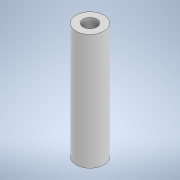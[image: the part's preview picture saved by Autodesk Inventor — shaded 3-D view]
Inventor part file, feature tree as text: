
AUTODESK INVENTOR PART (.ipt)
format: ipt  version: 2021 (Build 250183000, 183)  size: 94,208 bytes
history: native  units: mm
features: extrude x1, sketch x1
ambient origin geometry x8: Origin, YZ Plane, XZ Plane, XY Plane, X Axis, Y Axis, Z Axis, Center Point
bodies: Solid1 (feature_tree)
feature tree (2):
  extrude  "Extrusion1"  Depth=50.0mm
  sketch  "Sketch1"  dims[d0=6.0mm d1=12.0mm d2=50.0mm d3=0.0mm]
